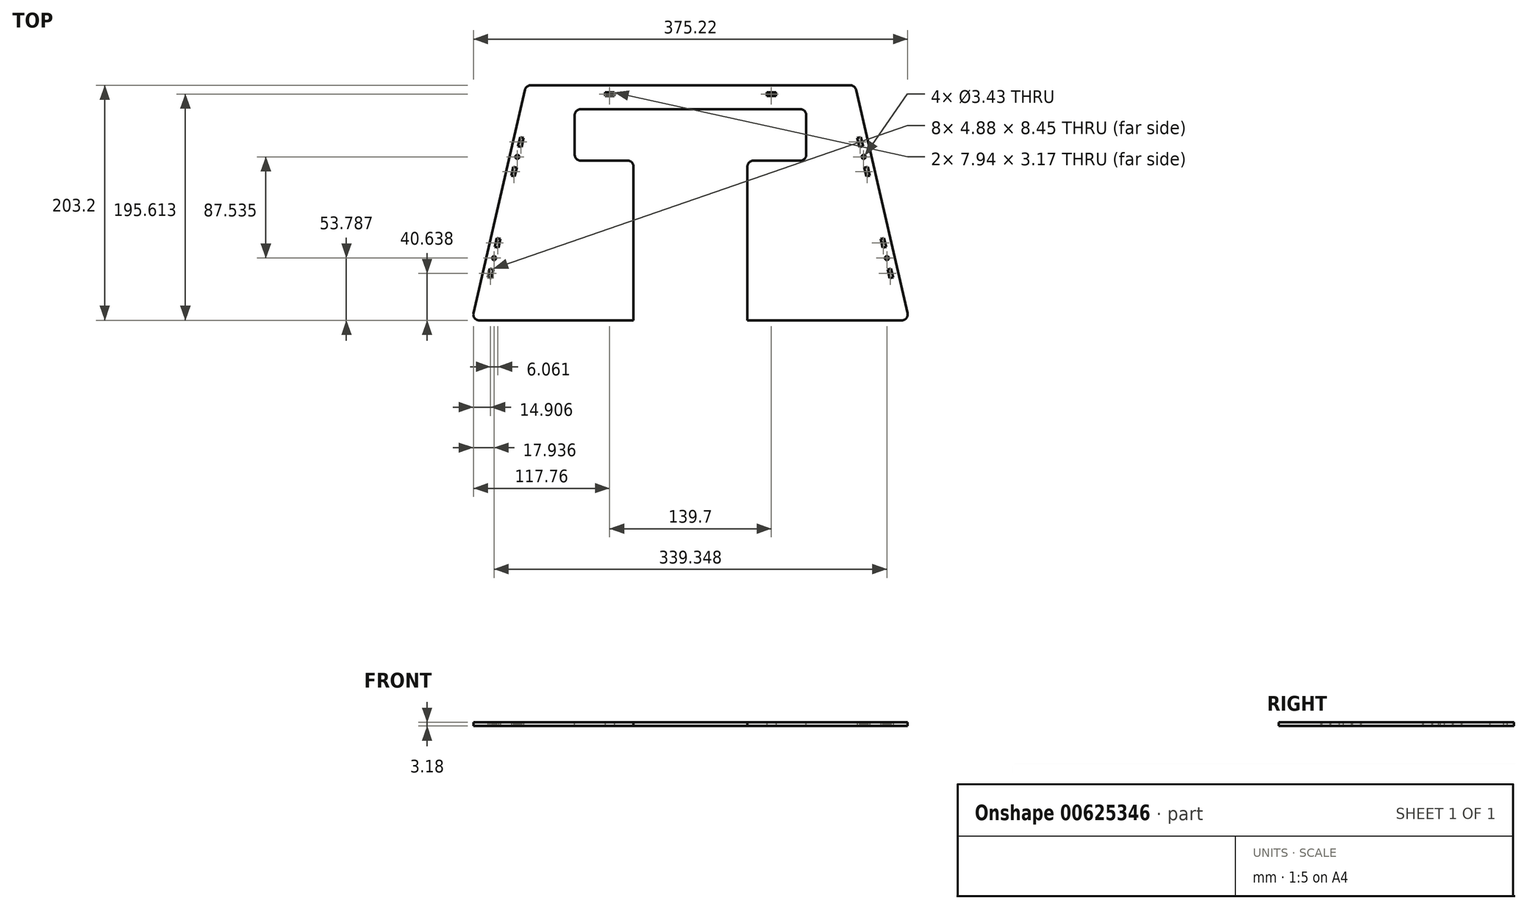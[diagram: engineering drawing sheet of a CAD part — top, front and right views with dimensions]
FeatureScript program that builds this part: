
annotation { "Feature Type Name" : "Feature", "Feature Type Description" : "" }
export const myFeature = defineFeature(function(context is Context, id is Id, definition is map)
    precondition{}
    {
        {
            var Q0;
            Q0=qCreatedBy(makeId("Top.planeOp"),FACE);
            var sketch = newSketch(context, id + "F0", { "sketchPlane" : qUnion([Q0])});
            skLineSegment(sketch, "E0", {"start": v(-188.91, -101.6) * mm, "end": v(-142.08, 101.6) * mm});
            skLineSegment(sketch, "E1", {"start": v(-142.08, 101.6) * mm, "end": v(142.08, 101.6) * mm});
            skLineSegment(sketch, "E2", {"start": v(142.08, 101.6) * mm, "end": v(188.91, -101.6) * mm});
            skLineSegment(sketch, "E3", {"start": v(188.91, -101.6) * mm, "end": v(-188.91, -101.6) * mm});
            skLineSegment(sketch, "E4", {"start": v(0, 101.6) * mm, "end": v(0, 0) * mm, "construction": true});
            skLineSegment(sketch, "E5.bottom", {"start": v(-65.88, 92.43) * mm, "end": v(-73.82, 92.43) * mm});
            skLineSegment(sketch, "E5.top", {"start": v(-65.88, 95.6) * mm, "end": v(-73.82, 95.6) * mm});
            skLineSegment(sketch, "E5.left", {"start": v(-65.88, 92.42) * mm, "end": v(-65.88, 95.6) * mm});
            skLineSegment(sketch, "E5.right", {"start": v(-73.82, 92.42) * mm, "end": v(-73.82, 95.6) * mm});
            skPoint(sketch, "E5.middle", {"position": v(-69.85, 94.01) * mm});
            skLineSegment(sketch, "E6", {"start": v(-136.87, 101.6) * mm, "end": v(-183.7, -101.6) * mm, "construction": true});
            skLineSegment(sketch, "E7", {"start": v(-148.99, 49) * mm, "end": v(-145.9, 48.3) * mm});
            skLineSegment(sketch, "E8", {"start": v(-144.11, 56.03) * mm, "end": v(-145.9, 48.3) * mm});
            skLineSegment(sketch, "E9", {"start": v(-144.11, 56.03) * mm, "end": v(-147.2, 56.74) * mm});
            skLineSegment(sketch, "E10", {"start": v(-148.99, 49) * mm, "end": v(-147.2, 56.74) * mm});
            skCircle(sketch, "E11", {"center": v(-149.58, 39.72) * mm, "radius": 1.71 * mm});
            skLineSegment(sketch, "E12", {"start": v(-147.44, 49) * mm, "end": v(-149.58, 39.72) * mm, "construction": true});
            skPoint(sketch, "E12.startSnap0", {"position": v(-147.44, 48.65) * mm});
            skLineSegment(sketch, "E13", {"start": v(-149.58, 39.72) * mm, "end": v(-156, 41.2) * mm, "construction": true});
            skLineSegment(sketch, "E14.MirrorCS", {"start": v(-151.8, 22.67) * mm, "end": v(-154.9, 23.38) * mm});
            skLineSegment(sketch, "E15.MirrorCS", {"start": v(-153.11, 31.12) * mm, "end": v(-150.02, 30.4) * mm});
            skLineSegment(sketch, "E16.MirrorCS", {"start": v(-153.11, 31.12) * mm, "end": v(-154.9, 23.38) * mm});
            skPoint(sketch, "E17.MirrorP", {"position": v(-151.57, 30.76) * mm});
            skLineSegment(sketch, "E18.MirrorCS", {"start": v(-151.8, 22.67) * mm, "end": v(-150.02, 30.4) * mm});
            skLineSegment(sketch, "E19", {"start": v(-175.14, -64.47) * mm, "end": v(-172.05, -65.19) * mm});
            skLineSegment(sketch, "E20", {"start": v(-172.05, -65.19) * mm, "end": v(-170.27, -57.45) * mm});
            skLineSegment(sketch, "E21", {"start": v(-170.27, -57.45) * mm, "end": v(-173.36, -56.74) * mm});
            skLineSegment(sketch, "E22", {"start": v(-173.36, -56.74) * mm, "end": v(-175.14, -64.47) * mm});
            skLineSegment(sketch, "E23", {"start": v(-167.3, -30.44) * mm, "end": v(-169.08, -38.18) * mm});
            skLineSegment(sketch, "E24", {"start": v(-169.08, -38.18) * mm, "end": v(-165.99, -38.89) * mm});
            skLineSegment(sketch, "E25", {"start": v(-165.99, -38.89) * mm, "end": v(-164.2, -31.15) * mm});
            skLineSegment(sketch, "E26", {"start": v(-164.2, -31.15) * mm, "end": v(-167.3, -30.44) * mm});
            skCircle(sketch, "E27", {"center": v(-169.67, -47.81) * mm, "radius": 1.71 * mm});
            skLineSegment(sketch, "E28", {"start": v(-171.81, -57.1) * mm, "end": v(-169.67, -47.81) * mm, "construction": true});
            skLineSegment(sketch, "E29", {"start": v(-169.67, -47.81) * mm, "end": v(-167.53, -38.53) * mm, "construction": true});
            skCircle(sketch, "E30.MirrorC", {"center": v(149.58, 39.72) * mm, "radius": 1.71 * mm});
            skLineSegment(sketch, "E31.MirrorCS", {"start": v(169.08, -38.18) * mm, "end": v(165.99, -38.89) * mm});
            skLineSegment(sketch, "E32.MirrorCS", {"start": v(153.11, 31.12) * mm, "end": v(150.02, 30.4) * mm});
            skCircle(sketch, "E33.MirrorC", {"center": v(169.67, -47.81) * mm, "radius": 1.71 * mm});
            skLineSegment(sketch, "E34.MirrorCS", {"start": v(169.67, -47.81) * mm, "end": v(167.53, -38.53) * mm, "construction": true});
            skLineSegment(sketch, "E35.MirrorCS", {"start": v(170.27, -57.45) * mm, "end": v(173.36, -56.74) * mm});
            skLineSegment(sketch, "E36.MirrorCS", {"start": v(165.99, -38.89) * mm, "end": v(164.2, -31.15) * mm});
            skLineSegment(sketch, "E37.MirrorCS", {"start": v(144.11, 56.03) * mm, "end": v(147.2, 56.74) * mm});
            skLineSegment(sketch, "E38.MirrorCS", {"start": v(144.11, 56.03) * mm, "end": v(145.9, 48.3) * mm});
            skLineSegment(sketch, "E39.MirrorCS", {"start": v(148.99, 49) * mm, "end": v(145.9, 48.3) * mm});
            skLineSegment(sketch, "E40.MirrorCS", {"start": v(148.99, 49) * mm, "end": v(147.2, 56.74) * mm});
            skLineSegment(sketch, "E41.MirrorCS", {"start": v(147.44, 49) * mm, "end": v(149.58, 39.72) * mm, "construction": true});
            skLineSegment(sketch, "E42.MirrorCS", {"start": v(153.11, 31.12) * mm, "end": v(154.9, 23.38) * mm});
            skLineSegment(sketch, "E43.MirrorCS", {"start": v(151.8, 22.67) * mm, "end": v(150.02, 30.4) * mm});
            skLineSegment(sketch, "E44.MirrorCS", {"start": v(164.2, -31.15) * mm, "end": v(167.3, -30.44) * mm});
            skLineSegment(sketch, "E45.MirrorCS", {"start": v(173.36, -56.74) * mm, "end": v(175.14, -64.47) * mm});
            skLineSegment(sketch, "E46.MirrorCS", {"start": v(175.14, -64.47) * mm, "end": v(172.05, -65.19) * mm});
            skLineSegment(sketch, "E47.MirrorCS", {"start": v(171.81, -57.1) * mm, "end": v(169.67, -47.81) * mm, "construction": true});
            skLineSegment(sketch, "E48.MirrorCS", {"start": v(172.05, -65.19) * mm, "end": v(170.27, -57.45) * mm});
            skLineSegment(sketch, "E49.MirrorCS", {"start": v(167.3, -30.44) * mm, "end": v(169.08, -38.18) * mm});
            skLineSegment(sketch, "E50.MirrorCS", {"start": v(151.8, 22.67) * mm, "end": v(154.9, 23.38) * mm});
            skLineSegment(sketch, "E51.MirrorCS", {"start": v(149.58, 39.72) * mm, "end": v(156, 41.2) * mm, "construction": true});
            skPoint(sketch, "E52.MirrorP", {"position": v(147.44, 48.65) * mm});
            skPoint(sketch, "E53.MirrorP", {"position": v(151.57, 30.76) * mm});
            skPoint(sketch, "E54.MirrorP", {"position": v(69.85, 94.01) * mm});
            skLineSegment(sketch, "E55.MirrorCS", {"start": v(65.88, 92.43) * mm, "end": v(73.82, 92.43) * mm});
            skLineSegment(sketch, "E56.MirrorCS", {"start": v(65.88, 95.6) * mm, "end": v(73.82, 95.6) * mm});
            skLineSegment(sketch, "E57.MirrorCS", {"start": v(65.88, 92.42) * mm, "end": v(65.88, 95.6) * mm});
            skLineSegment(sketch, "E58.MirrorCS", {"start": v(73.82, 92.42) * mm, "end": v(73.82, 95.6) * mm});
            skSolve(sketch);
        }
        {
            var Q0;
            Q0=qSketchRegion(id+"F0",true);
            extrude(context, id + "F1", {"entities" : qUnion([Q0]), "depth" : 3.17 * mm, "offsetDistance" : 25.4 * mm});
        }
        {
            var Q0;
            Q0=makeQuery(id+"F1.opExtrude","CAP_FACE",FACE,{"disambiguationData":[OSD([sQuery(id+"F0.wireOp",EDGE,"E0"),sQuery(id+"F0.wireOp",EDGE,"E1"),sQuery(id+"F0.wireOp",EDGE,"E2"),sQuery(id+"F0.wireOp",EDGE,"E3"),sQuery(id+"F0.wireOp",EDGE,"E5.bottom"),sQuery(id+"F0.wireOp",EDGE,"E5.top"),sQuery(id+"F0.wireOp",EDGE,"E5.left"),sQuery(id+"F0.wireOp",EDGE,"E5.right"),sQuery(id+"F0.wireOp",EDGE,"E7"),sQuery(id+"F0.wireOp",EDGE,"E8"),sQuery(id+"F0.wireOp",EDGE,"E9"),sQuery(id+"F0.wireOp",EDGE,"E10"),sQuery(id+"F0.wireOp",EDGE,"E11"),sQuery(id+"F0.wireOp",EDGE,"E14.MirrorCS"),sQuery(id+"F0.wireOp",EDGE,"E15.MirrorCS"),sQuery(id+"F0.wireOp",EDGE,"E16.MirrorCS"),sQuery(id+"F0.wireOp",EDGE,"E18.MirrorCS"),sQuery(id+"F0.wireOp",EDGE,"E19"),sQuery(id+"F0.wireOp",EDGE,"E20"),sQuery(id+"F0.wireOp",EDGE,"E21"),sQuery(id+"F0.wireOp",EDGE,"E22"),sQuery(id+"F0.wireOp",EDGE,"E23"),sQuery(id+"F0.wireOp",EDGE,"E24"),sQuery(id+"F0.wireOp",EDGE,"E25"),sQuery(id+"F0.wireOp",EDGE,"E26"),sQuery(id+"F0.wireOp",EDGE,"E27"),sQuery(id+"F0.wireOp",EDGE,"E30.MirrorC"),sQuery(id+"F0.wireOp",EDGE,"E31.MirrorCS"),sQuery(id+"F0.wireOp",EDGE,"E32.MirrorCS"),sQuery(id+"F0.wireOp",EDGE,"E33.MirrorC"),sQuery(id+"F0.wireOp",EDGE,"E35.MirrorCS"),sQuery(id+"F0.wireOp",EDGE,"E36.MirrorCS"),sQuery(id+"F0.wireOp",EDGE,"E37.MirrorCS"),sQuery(id+"F0.wireOp",EDGE,"E38.MirrorCS"),sQuery(id+"F0.wireOp",EDGE,"E39.MirrorCS"),sQuery(id+"F0.wireOp",EDGE,"E40.MirrorCS"),sQuery(id+"F0.wireOp",EDGE,"E42.MirrorCS"),sQuery(id+"F0.wireOp",EDGE,"E43.MirrorCS"),sQuery(id+"F0.wireOp",EDGE,"E44.MirrorCS"),sQuery(id+"F0.wireOp",EDGE,"E45.MirrorCS"),sQuery(id+"F0.wireOp",EDGE,"E46.MirrorCS"),sQuery(id+"F0.wireOp",EDGE,"E48.MirrorCS"),sQuery(id+"F0.wireOp",EDGE,"E49.MirrorCS"),sQuery(id+"F0.wireOp",EDGE,"E50.MirrorCS"),sQuery(id+"F0.wireOp",EDGE,"E55.MirrorCS"),sQuery(id+"F0.wireOp",EDGE,"E56.MirrorCS"),sQuery(id+"F0.wireOp",EDGE,"E57.MirrorCS"),sQuery(id+"F0.wireOp",EDGE,"E58.MirrorCS")])],"isStart":false});
            var sketch = newSketch(context, id + "F2", { "sketchPlane" : qUnion([Q0])});
            skLineSegment(sketch, "E59", {"start": v(0, 101.6) * mm, "end": v(0, 0) * mm, "construction": true});
            skLineSegment(sketch, "E60", {"start": v(-100.01, 80.96) * mm, "end": v(0, 80.96) * mm});
            skLineSegment(sketch, "E61", {"start": v(-100.01, 80.96) * mm, "end": v(-100.01, 36.51) * mm});
            skLineSegment(sketch, "E62", {"start": v(-100.01, 36.51) * mm, "end": v(-49.21, 36.51) * mm});
            skLineSegment(sketch, "E63", {"start": v(-49.21, 36.51) * mm, "end": v(-49.21, -101.6) * mm});
            skLineSegment(sketch, "E64", {"start": v(-49.21, -101.6) * mm, "end": v(0, -101.6) * mm});
            skLineSegment(sketch, "E65.MirrorCS", {"start": v(100.01, 80.96) * mm, "end": v(0, 80.96) * mm});
            skLineSegment(sketch, "E66.MirrorCS", {"start": v(100.01, 80.96) * mm, "end": v(100.01, 36.51) * mm});
            skLineSegment(sketch, "E67.MirrorCS", {"start": v(100.01, 36.51) * mm, "end": v(49.21, 36.51) * mm});
            skLineSegment(sketch, "E68.MirrorCS", {"start": v(49.21, 36.51) * mm, "end": v(49.21, -101.6) * mm});
            skLineSegment(sketch, "E69.MirrorCS", {"start": v(49.21, -101.6) * mm, "end": v(0, -101.6) * mm});
            skSolve(sketch);
        }
        {
            var Q0;
            Q0 = qSketchRegion(id + "F2", true);
            extrude(context, id + "F3", {"entities" : qUnion([Q0]), "operationType" : NewBodyOperationType.REMOVE, "endBound" : BoundingType.THROUGH_ALL, "oppositeDirection" : true, "depth" : 25.4 * mm, "offsetDistance" : 25.4 * mm});
        }
        {
            var Q0;
            Q0=makeQuery(id+"F1.opExtrude","SWEPT_EDGE",EDGE,{"disambiguationData":[OSD([sQuery(id+"F0.wireOp",EDGE,"E0"),sQuery(id+"F0.wireOp",EDGE,"E1")])]});
            var Q1;
            Q1=makeQuery(id+"F1.opExtrude","SWEPT_EDGE",EDGE,{"disambiguationData":[OSD([sQuery(id+"F0.wireOp",EDGE,"E0"),sQuery(id+"F0.wireOp",EDGE,"E3")])]});
            var Q2;
            Q2=makeQuery(id+"F1.opExtrude","SWEPT_EDGE",EDGE,{"disambiguationData":[OSD([sQuery(id+"F0.wireOp",EDGE,"E1"),sQuery(id+"F0.wireOp",EDGE,"E2")])]});
            var Q3;
            Q3=makeQuery(id+"F1.opExtrude","SWEPT_EDGE",EDGE,{"disambiguationData":[OSD([sQuery(id+"F0.wireOp",EDGE,"E2"),sQuery(id+"F0.wireOp",EDGE,"E3")])]});
            var Q4;
            Q4=makeQuery(id+"F3.boolean.opBoolean","COPY",EDGE,{"derivedFrom":makeQuery(id+"F3.opExtrude","SWEPT_EDGE",EDGE,{"disambiguationData":[OSD([sQuery(id+"F0.wireOp",EDGE,"E3"),sQuery(id+"F2.wireOp",EDGE,"E63"),sQuery(id+"F2.wireOp",EDGE,"E64")])]})});
            var Q5;
            Q5=makeQuery(id+"F3.boolean.opBoolean","COPY",EDGE,{"derivedFrom":makeQuery(id+"F3.opExtrude","SWEPT_EDGE",EDGE,{"disambiguationData":[OSD([sQuery(id+"F0.wireOp",EDGE,"E3"),sQuery(id+"F2.wireOp",EDGE,"E68.MirrorCS"),sQuery(id+"F2.wireOp",EDGE,"E69.MirrorCS")])]})});
            var Q6;
            Q6=makeQuery(id+"F3.boolean.opBoolean","COPY",EDGE,{"derivedFrom":makeQuery(id+"F3.opExtrude","SWEPT_EDGE",EDGE,{"disambiguationData":[OSD([sQuery(id+"F2.wireOp",EDGE,"E60"),sQuery(id+"F2.wireOp",EDGE,"E61")])]})});
            var Q7;
            Q7=makeQuery(id+"F3.boolean.opBoolean","COPY",EDGE,{"derivedFrom":makeQuery(id+"F3.opExtrude","SWEPT_EDGE",EDGE,{"disambiguationData":[OSD([sQuery(id+"F2.wireOp",EDGE,"E62"),sQuery(id+"F2.wireOp",EDGE,"E63")])]})});
            var Q8;
            Q8=makeQuery(id+"F3.boolean.opBoolean","COPY",EDGE,{"derivedFrom":makeQuery(id+"F3.opExtrude","SWEPT_EDGE",EDGE,{"disambiguationData":[OSD([sQuery(id+"F2.wireOp",EDGE,"E61"),sQuery(id+"F2.wireOp",EDGE,"E62")])]})});
            var Q9;
            Q9=makeQuery(id+"F3.boolean.opBoolean","COPY",EDGE,{"derivedFrom":makeQuery(id+"F3.opExtrude","SWEPT_EDGE",EDGE,{"disambiguationData":[OSD([sQuery(id+"F2.wireOp",EDGE,"E67.MirrorCS"),sQuery(id+"F2.wireOp",EDGE,"E68.MirrorCS")])]})});
            var Q10;
            Q10=makeQuery(id+"F3.boolean.opBoolean","COPY",EDGE,{"derivedFrom":makeQuery(id+"F3.opExtrude","SWEPT_EDGE",EDGE,{"disambiguationData":[OSD([sQuery(id+"F2.wireOp",EDGE,"E65.MirrorCS"),sQuery(id+"F2.wireOp",EDGE,"E66.MirrorCS")])]})});
            var Q11;
            Q11=makeQuery(id+"F3.boolean.opBoolean","COPY",EDGE,{"derivedFrom":makeQuery(id+"F3.opExtrude","SWEPT_EDGE",EDGE,{"disambiguationData":[OSD([sQuery(id+"F2.wireOp",EDGE,"E66.MirrorCS"),sQuery(id+"F2.wireOp",EDGE,"E67.MirrorCS")])]})});
            fillet(context, id + "F4", {"entities" : qUnion([Q0, Q1, Q2, Q3, Q4, Q5, Q6, Q7, Q8, Q9, Q10, Q11]), "radius" : 5.08 * mm, "tangentPropagation" : true, "allowEdgeOverflow" : false});
        }
    });
